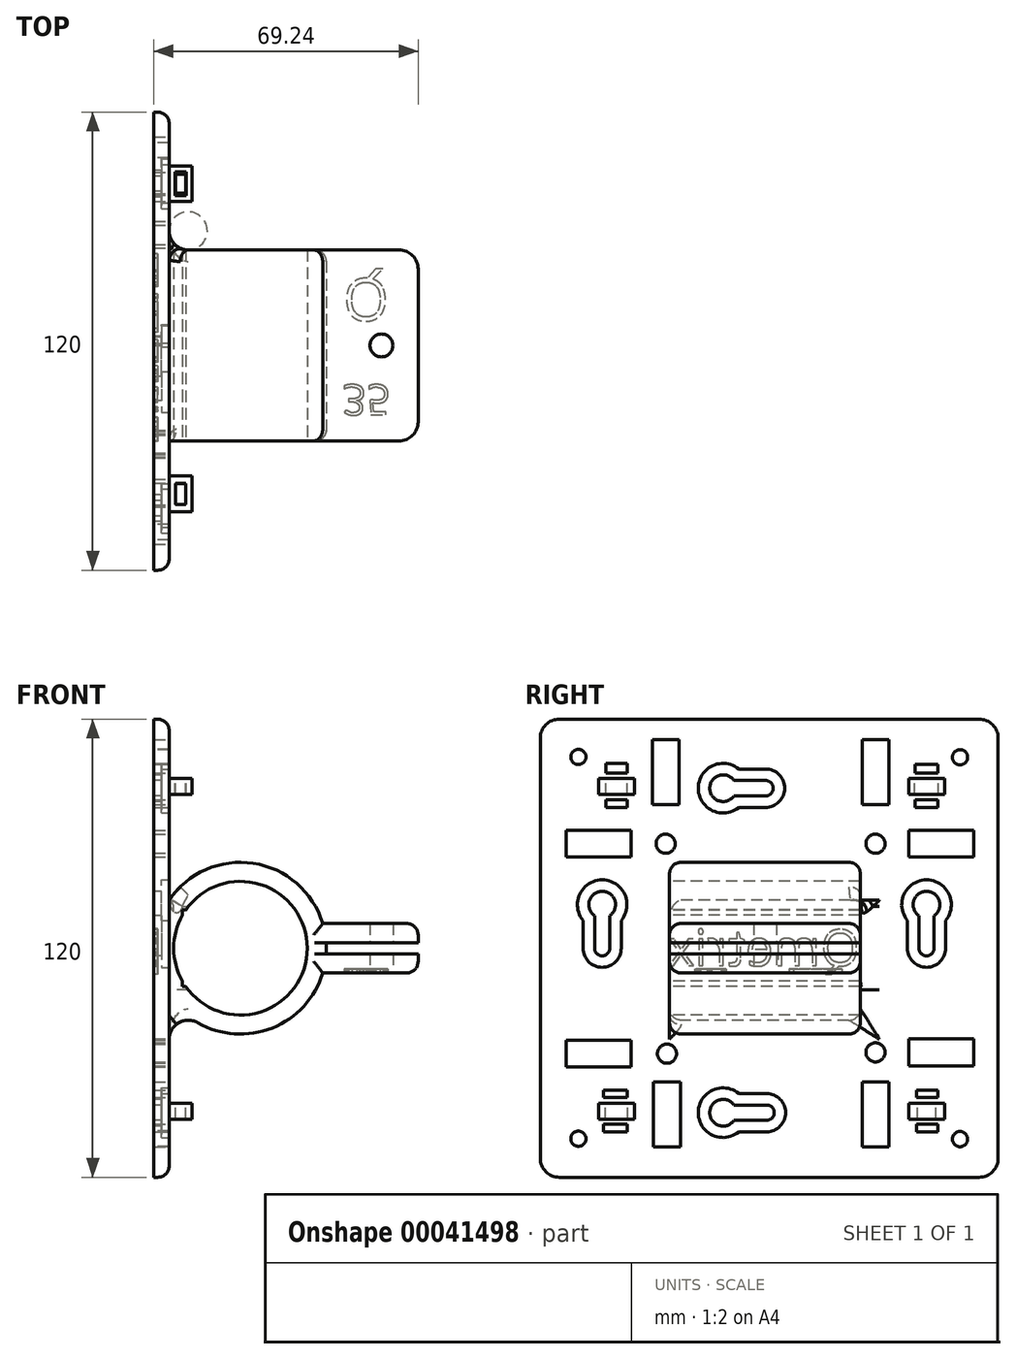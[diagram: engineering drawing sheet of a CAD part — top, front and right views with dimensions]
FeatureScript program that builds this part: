
annotation { "Feature Type Name" : "Feature", "Feature Type Description" : "" }
export const myFeature = defineFeature(function(context is Context, id is Id, definition is map)
    precondition{}
    {
        {
            var Q0;
            Q0=qCreatedBy(makeId("Top.planeOp"),FACE);
            var sketch = newSketch(context, id + "F0", { "sketchPlane" : qUnion([Q0])});
            skArc(sketch, "E0", {"start": v(-13.95, -1.23) * mm, "mid": v(13.99, 0.62) * mm, "end": v(-14, 0) * mm});
            skLineSegment(sketch, "E1.bottom", {"start": v(-14, 0) * mm, "end": v(-35.61, 0) * mm});
            skLineSegment(sketch, "E1.top", {"start": v(-17.8, 3.8) * mm, "end": v(-35.61, 3.8) * mm});
            skLineSegment(sketch, "E1.right", {"start": v(-35.61, 0) * mm, "end": v(-35.61, 3.8) * mm});
            skLineSegment(sketch, "E2.bottom", {"start": v(-13.95, -1.23) * mm, "end": v(-35.61, -1.23) * mm});
            skLineSegment(sketch, "E2.top", {"start": v(-17.57, -4.76) * mm, "end": v(-35.61, -4.76) * mm});
            skLineSegment(sketch, "E2.right", {"start": v(-35.61, -1.23) * mm, "end": v(-35.61, -4.76) * mm});
            skArc(sketch, "E3.trimOffspring", {"start": v(-17.57, -4.76) * mm, "mid": v(-1.54, -18.14) * mm, "end": v(16.51, -7.65) * mm});
            skLineSegment(sketch, "E4.bottom", {"start": v(16.51, 7.65) * mm, "end": v(17.36, 7.65) * mm});
            skLineSegment(sketch, "E4.top", {"start": v(16.51, -7.93) * mm, "end": v(17.36, -7.93) * mm});
            skLineSegment(sketch, "E4.left", {"start": v(16.51, -7.65) * mm, "end": v(16.51, -7.93) * mm});
            skLineSegment(sketch, "E4.right", {"start": v(17.36, 7.65) * mm, "end": v(17.36, -7.93) * mm});
            skArc(sketch, "E5.trimOffspring", {"start": v(16.51, 7.65) * mm, "mid": v(-2.03, 18.09) * mm, "end": v(-17.8, 3.8) * mm});
            skSolve(sketch);
        }
        {
            var Q0;
            Q0=makeQuery(id+"F0.imprint","IMPRINT",FACE,{"disambiguationData":[TD([[makeQuery(id+"F0.imprint","IMPRINT",EDGE,{"derivedFrom":sQuery(id+"F0.wireOp",EDGE,"E0")}),-1.0]])]});
            extrude(context, id + "F1", {"entities" : qUnion([Q0]), "depth" : 20 * mm});
        }
        {
            var Q0;
            Q0=makeQuery(id+"F1.opExtrude","SWEPT_FACE",FACE,{"disambiguationData":[OSD([sQuery(id+"F0.wireOp",EDGE,"E1.top")])]});
            var sketch = newSketch(context, id + "F2", { "sketchPlane" : qUnion([Q0])});
            skCircle(sketch, "E6", {"center": v(29.92, 10) * mm, "radius": 3 * mm});
            skPoint(sketch, "E6.centerSnap0", {"position": v(35.61, 10) * mm});
            skSolve(sketch);
        }
        {
            var Q0;
            Q0=makeQuery(id+"F2.imprint","IMPRINT",FACE,{"disambiguationData":[TD([[makeQuery(id+"F2.imprint","IMPRINT",EDGE,{"derivedFrom":sQuery(id+"F2.wireOp",EDGE,"E6")}),1.0]])]});
            extrude(context, id + "F3", {"entities" : qUnion([Q0]), "operationType" : NewBodyOperationType.REMOVE, "endBound" : BoundingType.THROUGH_ALL, "oppositeDirection" : true, "depth" : 25 * mm});
        }
        {
            var Q0;
            Q0=makeQuery(id+"F1.opExtrude","SWEPT_FACE",FACE,{"disambiguationData":[OSD([sQuery(id+"F0.wireOp",EDGE,"E4.bottom")])]});
            var sketch = newSketch(context, id + "F4", { "sketchPlane" : qUnion([Q0])});
            skCircle(sketch, "E7", {"center": v(-31.76, 10) * mm, "radius": 22.5 * mm});
            skPoint(sketch, "E7.centerSnap0", {"position": v(-17.36, 10) * mm});
            skCircle(sketch, "E8", {"center": v(-31.76, 10) * mm, "radius": 17.5 * mm});
            skSolve(sketch);
        }
        {
            var Q0;
            {var subQ0=sQuery(id+"F0.wireOp",EDGE,"E4.bottom");var subQ1=makeQuery(id+"F1.opExtrude","CAP_EDGE",EDGE,{"disambiguationData":[OSD([subQ0])],"isStart":true});var subQ9=sQuery(id+"F4.wireOp",EDGE,"E7");var subQ10=makeQuery(id+"F4.imprint","INTERSECT",VERTEX,{"derivedFrom":[subQ1,subQ9]});Q0=makeQuery(id+"F4.imprint","IMPRINT",FACE,{"disambiguationData":[TD([[makeQuery(id+"F4.imprint","IMPRINT",EDGE,{"disambiguationData":[TD([[subQ10,1.0]])],"derivedFrom":subQ9}),1.0]])]});}
            var Q1;
            {var subQ0=sQuery(id+"F0.wireOp",EDGE,"E4.bottom");var subQ7=makeQuery(id+"F1.opExtrude","CAP_EDGE",EDGE,{"disambiguationData":[OSD([subQ0])],"isStart":true});var subQ9=sQuery(id+"F4.wireOp",EDGE,"E7");var subQ10=makeQuery(id+"F4.imprint","INTERSECT",VERTEX,{"derivedFrom":[subQ7,subQ9]});Q1=makeQuery(id+"F4.imprint","IMPRINT",FACE,{"disambiguationData":[TD([[makeQuery(id+"F4.imprint","IMPRINT",EDGE,{"disambiguationData":[TD([[subQ10,-1.0]])],"derivedFrom":subQ9}),1.0]])]});}
            var Q2;
            Q2=sQuery(id+"F4.wireOp",EDGE,"E7");
            extrude(context, id + "F5", {"entities" : qUnion([Q0, Q1]), "operationType" : NewBodyOperationType.ADD, "surfaceEntities" : qUnion([Q2]), "depth" : 35 * mm, "symmetric" : true});
        }
        {
            var Q0;
            Q0=makeQuery(id+"F5.boolean.opBoolean","SPLIT",FACE,{"disambiguationData":[TD([makeQuery(id+"F1.opExtrude","SWEPT_FACE",FACE,{"disambiguationData":[OSD([sQuery(id+"F0.wireOp",EDGE,"E4.right")])]})])],"derivedFrom":makeQuery(id+"F1.opExtrude","SWEPT_FACE",FACE,{"disambiguationData":[OSD([sQuery(id+"F0.wireOp",EDGE,"E4.top")])]})});
            extrude(context, id + "F6", {"entities" : qUnion([Q0]), "operationType" : NewBodyOperationType.REMOVE, "oppositeDirection" : true, "depth" : 25 * mm});
        }
        {
            var Q0;
            Q0=makeQuery(id+"F5.opExtrude","CAP_FACE",FACE,{"disambiguationData":[OSD([sQuery(id+"F4.wireOp",EDGE,"E7"),sQuery(id+"F4.wireOp",EDGE,"E8")])],"isStart":true});
            var sketch = newSketch(context, id + "F7", { "sketchPlane" : qUnion([Q0])});
            skLineSegment(sketch, "E9.bottom", {"start": v(49.2, 8.53) * mm, "end": v(78.32, 8.53) * mm});
            skLineSegment(sketch, "E9.top", {"start": v(49.2, 3.53) * mm, "end": v(78.32, 3.53) * mm});
            skLineSegment(sketch, "E9.left", {"start": v(49.2, 8.53) * mm, "end": v(49.2, 3.53) * mm});
            skLineSegment(sketch, "E9.right", {"start": v(78.32, 8.53) * mm, "end": v(78.32, 3.53) * mm});
            skPoint(sketch, "E10.oppositeSnap0", {"position": v(78.32, 6.03) * mm});
            skLineSegment(sketch, "E10.bottom", {"start": v(49.2, 11.47) * mm, "end": v(78.32, 11.47) * mm});
            skLineSegment(sketch, "E10.top", {"start": v(49.2, 16.47) * mm, "end": v(78.32, 16.47) * mm});
            skLineSegment(sketch, "E10.left", {"start": v(49.2, 11.47) * mm, "end": v(49.2, 16.47) * mm});
            skLineSegment(sketch, "E10.right", {"start": v(78.32, 11.47) * mm, "end": v(78.32, 16.47) * mm});
            skLineSegment(sketch, "E11.bottom", {"start": v(56.42, 8.53) * mm, "end": v(46.21, 8.53) * mm});
            skLineSegment(sketch, "E11.top", {"start": v(56.42, 11.47) * mm, "end": v(46.21, 11.47) * mm});
            skLineSegment(sketch, "E11.left", {"start": v(56.42, 8.53) * mm, "end": v(56.42, 11.47) * mm});
            skLineSegment(sketch, "E11.right", {"start": v(46.21, 8.53) * mm, "end": v(46.21, 11.47) * mm});
            skSolve(sketch);
        }
        {
            var Q0;
            {var subQ0=sQuery(id+"F7.wireOp",EDGE,"E11.bottom");var subQ3=makeQuery(id+"F5.opExtrude","CAP_EDGE",EDGE,{"disambiguationData":[OSD([sQuery(id+"F4.wireOp",EDGE,"E7")])],"isStart":true});var subQ4=makeQuery(id+"F7.imprint","INTERSECT",VERTEX,{"derivedFrom":[subQ3,subQ0]});Q0=makeQuery(id+"F7.imprint","IMPRINT",FACE,{"disambiguationData":[TD([[makeQuery(id+"F7.imprint","IMPRINT",EDGE,{"disambiguationData":[TD([[subQ4,1.0]])],"derivedFrom":subQ3}),-1.0]])]});}
            var Q1;
            Q1=makeQuery(id+"F5.opExtrude","CAP_FACE",FACE,{"disambiguationData":[OSD([sQuery(id+"F4.wireOp",EDGE,"E7"),sQuery(id+"F4.wireOp",EDGE,"E8")])],"isStart":false});
            extrude(context, id + "F8", {"entities" : qUnion([Q0]), "operationType" : NewBodyOperationType.REMOVE, "endBound" : BoundingType.UP_TO_SURFACE, "oppositeDirection" : true, "endBoundEntityFace" : qUnion([Q1]), "depth" : 25 * mm});
        }
        {
            var Q0;
            {var subQ0=sQuery(id+"F7.wireOp",EDGE,"E9.right");Q0=makeQuery(id+"F7.imprint","IMPRINT",FACE,{"disambiguationData":[TD([[makeQuery(id+"F7.imprint","IMPRINT",EDGE,{"derivedFrom":subQ0}),-1.0]])]});}
            var Q1;
            {var subQ0=sQuery(id+"F7.wireOp",EDGE,"E10.right");Q1=makeQuery(id+"F7.imprint","IMPRINT",FACE,{"disambiguationData":[TD([[makeQuery(id+"F7.imprint","IMPRINT",EDGE,{"derivedFrom":subQ0}),1.0]])]});}
            var Q2;
            Q2=makeQuery(id+"F5.opExtrude","CAP_FACE",FACE,{"disambiguationData":[OSD([sQuery(id+"F4.wireOp",EDGE,"E7"),sQuery(id+"F4.wireOp",EDGE,"E8")])],"isStart":false});
            extrude(context, id + "F9", {"entities" : qUnion([Q0, Q1]), "operationType" : NewBodyOperationType.ADD, "endBound" : BoundingType.UP_TO_SURFACE, "oppositeDirection" : true, "endBoundEntityFace" : qUnion([Q2]), "depth" : 25 * mm});
        }
        {
            var Q0;
            {var subQ0=sQuery(id+"F7.wireOp",EDGE,"E11.top");var subQ1=sQuery(id+"F4.wireOp",EDGE,"E7");var subQ2=sQuery(id+"F4.wireOp",EDGE,"E8");var subQ3=sQuery(id+"F0.wireOp",EDGE,"E4.right");var subQ4=sQuery(id+"F0.wireOp",EDGE,"E4.bottom");var subQ9=sQuery(id+"F0.wireOp",EDGE,"E3.trimOffspring");var subQ10=makeQuery(id+"F1.opExtrude","SWEPT_FACE",FACE,{"disambiguationData":[OSD([subQ9])]});var subQ12=sQuery(id+"F0.wireOp",EDGE,"E5.trimOffspring");var subQ36=makeQuery(id+"F5.boolean.opBoolean","SPLIT",FACE,{"disambiguationData":[TD([subQ10])],"derivedFrom":makeQuery(id+"F5.opExtrude","CAP_FACE",FACE,{"disambiguationData":[OSD([subQ4,subQ3,subQ12,subQ1,subQ2])],"isStart":true})});var subQ37=sQuery(id+"F7.wireOp",EDGE,"E11.bottom");Q0=qUnion([makeQuery(id+"F9.boolean.opBoolean","MERGE",FACE,{"derivedFrom":[makeQuery(id+"F8.boolean.opBoolean","SPLIT",FACE,{"disambiguationData":[TD([makeQuery(id+"F8.opExtrude","SWEPT_FACE",FACE,{"disambiguationData":[OSD([subQ37])]})])],"derivedFrom":subQ36}),makeQuery(id+"F9.opExtrude","CAP_FACE",FACE,{"disambiguationData":[OSD([subQ1,sQuery(id+"F7.wireOp",EDGE,"E9.bottom"),sQuery(id+"F7.wireOp",EDGE,"E9.top"),sQuery(id+"F7.wireOp",EDGE,"E9.right"),subQ37])],"isStart":true})]}),makeQuery(id+"F9.boolean.opBoolean","MERGE",FACE,{"derivedFrom":[makeQuery(id+"F8.boolean.opBoolean","SPLIT",FACE,{"disambiguationData":[TD([makeQuery(id+"F8.opExtrude","SWEPT_FACE",FACE,{"disambiguationData":[OSD([subQ0])]})])],"derivedFrom":subQ36}),makeQuery(id+"F9.opExtrude","CAP_FACE",FACE,{"disambiguationData":[OSD([subQ1,sQuery(id+"F7.wireOp",EDGE,"E10.bottom"),sQuery(id+"F7.wireOp",EDGE,"E10.top"),sQuery(id+"F7.wireOp",EDGE,"E10.right"),subQ0])],"isStart":true})]})]);}
            extrude(context, id + "F10", {"entities" : qUnion([Q0]), "operationType" : NewBodyOperationType.ADD, "depth" : 15 * mm});
        }
        {
            var Q0;
            {var subQ0=sQuery(id+"F7.wireOp",EDGE,"E9.top");Q0=makeQuery(id+"F10.boolean.opBoolean","MERGE",FACE,{"derivedFrom":[makeQuery(id+"F9.opExtrude","SWEPT_FACE",FACE,{"disambiguationData":[OSD([subQ0])]}),makeQuery(id+"F10.opExtrude","SWEPT_FACE",FACE,{"disambiguationData":[OSD([subQ0])]})]});}
            var sketch = newSketch(context, id + "F11", { "sketchPlane" : qUnion([Q0])});
            skCircle(sketch, "E12", {"center": v(68.71, -0.15) * mm, "radius": 3 * mm});
            skPoint(sketch, "E12.centerSnap0", {"position": v(78.32, -0.15) * mm});
            skSolve(sketch);
        }
        {
            var Q0;
            Q0=makeQuery(id+"F1.opExtrude","CAP_EDGE",EDGE,{"disambiguationData":[OSD([sQuery(id+"F0.wireOp",EDGE,"E2.right")])],"isStart":true});
            var Q1;
            Q1=makeQuery(id+"F1.opExtrude","CAP_EDGE",EDGE,{"disambiguationData":[OSD([sQuery(id+"F0.wireOp",EDGE,"E1.right")])],"isStart":true});
            var Q2;
            Q2=makeQuery(id+"F1.opExtrude","CAP_EDGE",EDGE,{"disambiguationData":[OSD([sQuery(id+"F0.wireOp",EDGE,"E2.right")])],"isStart":false});
            var Q3;
            Q3=makeQuery(id+"F1.opExtrude","CAP_EDGE",EDGE,{"disambiguationData":[OSD([sQuery(id+"F0.wireOp",EDGE,"E1.right")])],"isStart":false});
            var Q4;
            Q4=makeQuery(id+"F9.opExtrude","CAP_EDGE",EDGE,{"disambiguationData":[OSD([sQuery(id+"F7.wireOp",EDGE,"E9.right")])],"isStart":true});
            var Q5;
            Q5=makeQuery(id+"F9.opExtrude","CAP_EDGE",EDGE,{"disambiguationData":[OSD([sQuery(id+"F7.wireOp",EDGE,"E10.right")])],"isStart":true});
            var Q6;
            Q6=makeQuery(id+"F9.opExtrude","CAP_EDGE",EDGE,{"disambiguationData":[OSD([sQuery(id+"F7.wireOp",EDGE,"E10.right")])],"isStart":false});
            var Q7;
            Q7=makeQuery(id+"F9.opExtrude","CAP_EDGE",EDGE,{"disambiguationData":[OSD([sQuery(id+"F7.wireOp",EDGE,"E9.right")])],"isStart":false});
            var Q8;
            Q8=makeQuery(id+"F10.opExtrude","CAP_EDGE",EDGE,{"disambiguationData":[OSD([sQuery(id+"F7.wireOp",EDGE,"E9.right")])],"isStart":false});
            var Q9;
            Q9=makeQuery(id+"F10.opExtrude","CAP_EDGE",EDGE,{"disambiguationData":[OSD([sQuery(id+"F7.wireOp",EDGE,"E10.right")])],"isStart":false});
            fillet(context, id + "F12", {"entities" : qUnion([Q0, Q1, Q2, Q3, Q4, Q5, Q6, Q7, Q8, Q9]), "radius" : 5 * mm, "tangentPropagation" : true, "allowEdgeOverflow" : false});
        }
        {
            var Q0;
            {var subQ0=sQuery(id+"F7.wireOp",EDGE,"E9.top");Q0=makeQuery(id+"F10.boolean.opBoolean","MERGE",FACE,{"derivedFrom":[makeQuery(id+"F9.opExtrude","SWEPT_FACE",FACE,{"disambiguationData":[OSD([subQ0])]}),makeQuery(id+"F10.opExtrude","SWEPT_FACE",FACE,{"disambiguationData":[OSD([subQ0])]})]});}
            var sketch = newSketch(context, id + "F13", { "sketchPlane" : qUnion([Q0])});
            skText(sketch, "E13", { "text": "35", "fontName": "OpenSans-Regular.ttf"});
            skText(sketch, "E14", { "text": "Q", "fontName": "OpenSans-Regular.ttf"});
            const initialGuessF13  = {"E13": [0.0584, 0.01015, 1, 0, 0.00796], "E14": [0.05865, -0.01766, 1, 0, 0.0111]};
            skSetInitialGuess(sketch, initialGuessF13);
            skSolve(sketch);
        }
        {
            var Q0;
            Q0=makeQuery(id+"F0.imprint","IMPRINT",FACE,{"disambiguationData":[TD([[makeQuery(id+"F0.imprint","IMPRINT",EDGE,{"derivedFrom":sQuery(id+"F0.wireOp",EDGE,"E0")}),-1.0]])]});
            var sketch = newSketch(context, id + "F14", { "sketchPlane" : qUnion([Q0])});
            skLineSegment(sketch, "E15.bottom", {"start": v(13.08, 61.27) * mm, "end": v(9.08, 61.27) * mm});
            skLineSegment(sketch, "E15.top", {"start": v(13.08, -58.73) * mm, "end": v(9.08, -58.73) * mm});
            skLineSegment(sketch, "E15.left", {"start": v(13.08, 61.27) * mm, "end": v(13.08, -58.73) * mm});
            skLineSegment(sketch, "E15.right", {"start": v(9.08, 61.27) * mm, "end": v(9.08, -58.73) * mm});
            skSolve(sketch);
        }
        {
            var Q0;
            Q0=makeQuery(id+"F0.imprint","IMPRINT",FACE,{"disambiguationData":[TD([[makeQuery(id+"F0.imprint","IMPRINT",EDGE,{"derivedFrom":sQuery(id+"F0.wireOp",EDGE,"E0")}),-1.0]])]});
            extrude(context, id + "F15", {"entities" : qUnion([Q0]), "operationType" : NewBodyOperationType.REMOVE, "depth" : 25 * mm});
        }
        {
            var Q0;
            {var subQ0=sQuery(id+"F14.wireOp",EDGE,"E15.top");Q0=makeQuery(id+"F14.imprint","IMPRINT",FACE,{"disambiguationData":[TD([[makeQuery(id+"F14.imprint","IMPRINT",EDGE,{"derivedFrom":subQ0}),-1.0]])]});}
            var Q1;
            {var subQ0=sQuery(id+"F14.wireOp",EDGE,"E15.bottom");Q1=makeQuery(id+"F14.imprint","IMPRINT",FACE,{"disambiguationData":[TD([[makeQuery(id+"F14.imprint","IMPRINT",EDGE,{"derivedFrom":subQ0}),1.0]])]});}
            var Q2;
            {var subQ0=sQuery(id+"F14.wireOp",EDGE,"E15.left");var subQ1=makeQuery(id+"F0.imprint","IMPRINT",EDGE,{"derivedFrom":sQuery(id+"F0.wireOp",EDGE,"E4.bottom")});var subQ2=makeQuery(id+"F14.imprint","INTERSECT",VERTEX,{"derivedFrom":[subQ1,subQ0]});Q2=makeQuery(id+"F14.imprint","IMPRINT",FACE,{"disambiguationData":[TD([[makeQuery(id+"F14.imprint","IMPRINT",EDGE,{"disambiguationData":[TD([[subQ2,-1.0]])],"derivedFrom":subQ0}),-1.0]])]});}
            extrude(context, id + "F16", {"entities" : qUnion([Q0, Q1, Q2]), "operationType" : NewBodyOperationType.ADD, "depth" : 70 * mm, "hasSecondDirection" : true, "secondDirectionOppositeDirection" : true, "secondDirectionDepth" : 50 * mm});
        }
        {
            var Q0;
            Q0=makeQuery(id+"F16.opExtrude","CAP_EDGE",EDGE,{"disambiguationData":[OSD([sQuery(id+"F14.wireOp",EDGE,"E15.bottom")])],"isStart":false});
            var Q1;
            Q1=makeQuery(id+"F16.opExtrude","CAP_EDGE",EDGE,{"disambiguationData":[OSD([sQuery(id+"F14.wireOp",EDGE,"E15.bottom")])],"isStart":true});
            var Q2;
            Q2=makeQuery(id+"F16.opExtrude","CAP_EDGE",EDGE,{"disambiguationData":[OSD([sQuery(id+"F14.wireOp",EDGE,"E15.top")])],"isStart":true});
            var Q3;
            Q3=makeQuery(id+"F16.opExtrude","CAP_EDGE",EDGE,{"disambiguationData":[OSD([sQuery(id+"F14.wireOp",EDGE,"E15.top")])],"isStart":false});
            fillet(context, id + "F17", {"entities" : qUnion([Q0, Q1, Q2, Q3]), "radius" : 5 * mm, "tangentPropagation" : true, "allowEdgeOverflow" : false});
        }
        {
            var Q0;
            Q0=makeQuery(id+"F16.opExtrude","SWEPT_FACE",FACE,{"disambiguationData":[OSD([sQuery(id+"F14.wireOp",EDGE,"E15.right")])]});
            var sketch = newSketch(context, id + "F18", { "sketchPlane" : qUnion([Q0])});
            skCircle(sketch, "E16", {"center": v(-51.27, -40) * mm, "radius": 2 * mm});
            skCircle(sketch, "E17", {"center": v(-51.27, 60) * mm, "radius": 2 * mm});
            skCircle(sketch, "E18", {"center": v(48.73, -39.9) * mm, "radius": 2 * mm});
            skCircle(sketch, "E19", {"center": v(48.73, 60.1) * mm, "radius": 2 * mm});
            skLineSegment(sketch, "E20", {"start": v(-82.64, 10) * mm, "end": v(82.64, 10) * mm, "construction": true});
            skArc(sketch, "E21", {"start": v(-44.5, 10) * mm, "mid": v(-42.5, 8) * mm, "end": v(-40.5, 10) * mm});
            skArc(sketch, "E22", {"start": v(40.5, 10) * mm, "mid": v(42.5, 8) * mm, "end": v(44.5, 10) * mm});
            skLineSegment(sketch, "E23", {"start": v(-82.64, 21.4) * mm, "end": v(68.31, 21.4) * mm, "construction": true});
            skArc(sketch, "E24", {"start": v(-40.5, 18.53) * mm, "mid": v(-42.5, 24.9) * mm, "end": v(-44.5, 18.53) * mm});
            skArc(sketch, "E25", {"start": v(44.5, 18.53) * mm, "mid": v(42.5, 24.9) * mm, "end": v(40.5, 18.53) * mm});
            skLineSegment(sketch, "E26", {"start": v(-44.5, 10) * mm, "end": v(-44.5, 18.53) * mm});
            skLineSegment(sketch, "E27", {"start": v(-40.5, 10) * mm, "end": v(-40.5, 18.53) * mm});
            skLineSegment(sketch, "E28", {"start": v(40.5, 10) * mm, "end": v(40.5, 18.53) * mm});
            skLineSegment(sketch, "E29", {"start": v(44.5, 10) * mm, "end": v(44.5, 18.53) * mm});
            skLineSegment(sketch, "E30.1.0", {"start": v(0, 53.91) * mm, "end": v(7.95, 53.91) * mm});
            skArc(sketch, "E30.1.1", {"start": v(7.95, 49.91) * mm, "mid": v(14.32, 51.91) * mm, "end": v(7.95, 53.91) * mm});
            skLineSegment(sketch, "E30.1.2", {"start": v(-0.59, 49.91) * mm, "end": v(7.95, 49.91) * mm});
            skArc(sketch, "E30.1.3", {"start": v(0, 53.91) * mm, "mid": v(-2.3, 52.2) * mm, "end": v(-0.59, 49.91) * mm});
            skArc(sketch, "E30.1.12", {"start": v(-0.59, -31.09) * mm, "mid": v(-2.59, -33.09) * mm, "end": v(-0.59, -35.09) * mm});
            skLineSegment(sketch, "E30.1.13", {"start": v(-0.59, -31.09) * mm, "end": v(7.95, -31.09) * mm});
            skLineSegment(sketch, "E30.1.14", {"start": v(-0.59, -35.09) * mm, "end": v(7.95, -35.09) * mm});
            skArc(sketch, "E30.1.15", {"start": v(7.95, -35.09) * mm, "mid": v(14.32, -33.09) * mm, "end": v(7.95, -31.09) * mm});
            skPoint(sketch, "E30.center", {"position": v(0, 10) * mm});
            skLineSegment(sketch, "E30.anchor1", {"start": v(0, 10) * mm, "end": v(-44.5, 10) * mm, "construction": true});
            skLineSegment(sketch, "E30.anchor2", {"start": v(0, 10) * mm, "end": v(0, 53.91) * mm, "construction": true});
            skPoint(sketch, "E31.MirrorCS.end.orphan", {"position": v(-44.5, -18.53) * mm});
            skPoint(sketch, "E31.MirrorCS.start.orphan", {"position": v(-40.5, -18.53) * mm});
            skPoint(sketch, "E32.MirrorCS.start.orphan", {"position": v(-44.5, -10) * mm});
            skPoint(sketch, "E33.MirrorCS.start.orphan", {"position": v(-40.5, -10) * mm});
            skPoint(sketch, "E34.MirrorCS.end.orphan", {"position": v(40.5, -18.53) * mm});
            skPoint(sketch, "E34.MirrorCS.start.orphan", {"position": v(44.5, -18.53) * mm});
            skPoint(sketch, "E35.MirrorCS.start.orphan", {"position": v(44.5, -10) * mm});
            skPoint(sketch, "E36.MirrorCS.start.orphan", {"position": v(40.5, -10) * mm});
            skCircle(sketch, "E37.1.0.0", {"center": v(-26.27, -40) * mm, "radius": 2 * mm});
            skCircle(sketch, "E37.2.0.0", {"center": v(-1.27, -40) * mm, "radius": 2 * mm});
            skCircle(sketch, "E37.3.0.0", {"center": v(23.73, -40) * mm, "radius": 2 * mm});
            skLineSegment(sketch, "E37.direction1", {"start": v(-51.27, -40) * mm, "end": v(-26.27, -40) * mm, "construction": true});
            skCircle(sketch, "E38.0.1.0", {"center": v(-51.27, -15) * mm, "radius": 2 * mm});
            skCircle(sketch, "E38.0.2.0", {"center": v(-51.27, 10) * mm, "radius": 2 * mm});
            skCircle(sketch, "E38.0.3.0", {"center": v(-51.27, 35) * mm, "radius": 2 * mm});
            skLineSegment(sketch, "E38.direction2", {"start": v(-51.27, -40) * mm, "end": v(-51.27, -15) * mm, "construction": true});
            skSolve(sketch);
        }
        {
            var Q0;
            Q0=makeQuery(id+"F18.imprint","IMPRINT",FACE,{"disambiguationData":[TD([[makeQuery(id+"F18.imprint","IMPRINT",EDGE,{"derivedFrom":sQuery(id+"F18.wireOp",EDGE,"E18")}),1.0]])]});
            var Q1;
            Q1=makeQuery(id+"F18.imprint","IMPRINT",FACE,{"disambiguationData":[TD([[makeQuery(id+"F18.imprint","IMPRINT",EDGE,{"derivedFrom":sQuery(id+"F18.wireOp",EDGE,"E16")}),1.0]])]});
            var Q2;
            Q2=makeQuery(id+"F18.imprint","IMPRINT",FACE,{"disambiguationData":[TD([[makeQuery(id+"F18.imprint","IMPRINT",EDGE,{"derivedFrom":sQuery(id+"F18.wireOp",EDGE,"E17")}),1.0]])]});
            var Q3;
            Q3=makeQuery(id+"F18.imprint","IMPRINT",FACE,{"disambiguationData":[TD([[makeQuery(id+"F18.imprint","IMPRINT",EDGE,{"derivedFrom":sQuery(id+"F18.wireOp",EDGE,"E19")}),1.0]])]});
            var Q4;
            Q4=makeQuery(id+"F18.imprint","IMPRINT",FACE,{"disambiguationData":[TD([[makeQuery(id+"F18.imprint","IMPRINT",EDGE,{"derivedFrom":sQuery(id+"F18.wireOp",EDGE,"E21")}),1.0]])]});
            var Q5;
            Q5=makeQuery(id+"F18.imprint","IMPRINT",FACE,{"disambiguationData":[TD([[makeQuery(id+"F18.imprint","IMPRINT",EDGE,{"derivedFrom":sQuery(id+"F18.wireOp",EDGE,"E30.1.12")}),1.0]])]});
            var Q6;
            Q6=makeQuery(id+"F18.imprint","IMPRINT",FACE,{"disambiguationData":[TD([[makeQuery(id+"F18.imprint","IMPRINT",EDGE,{"derivedFrom":sQuery(id+"F18.wireOp",EDGE,"E22")}),1.0]])]});
            var Q7;
            Q7=makeQuery(id+"F18.imprint","IMPRINT",FACE,{"disambiguationData":[TD([[makeQuery(id+"F18.imprint","IMPRINT",EDGE,{"derivedFrom":sQuery(id+"F18.wireOp",EDGE,"E30.1.0")}),-1.0]])]});
            var Q8;
            Q8=sQuery(id+"F18.wireOp",EDGE,"E16");
            var Q9;
            Q9=sQuery(id+"F18.wireOp",EDGE,"E17");
            var Q10;
            Q10=sQuery(id+"F18.wireOp",EDGE,"E19");
            var Q11;
            Q11=sQuery(id+"F18.wireOp",EDGE,"E18");
            extrude(context, id + "F19", {"entities" : qUnion([Q0, Q1, Q2, Q3, Q4, Q5, Q6, Q7]), "operationType" : NewBodyOperationType.REMOVE, "surfaceEntities" : qUnion([Q8, Q9, Q10, Q11]), "oppositeDirection" : true, "depth" : 25 * mm});
        }
        {
            var Q0;
            {var subQ0=sQuery(id+"F4.wireOp",EDGE,"E7");Q0=makeQuery(id+"F9.boolean.opBoolean","MERGE",FACE,{"derivedFrom":[makeQuery(id+"F5.opExtrude","CAP_FACE",FACE,{"disambiguationData":[OSD([sQuery(id+"F0.wireOp",EDGE,"E4.bottom"),sQuery(id+"F0.wireOp",EDGE,"E4.right"),sQuery(id+"F0.wireOp",EDGE,"E5.trimOffspring"),subQ0,sQuery(id+"F4.wireOp",EDGE,"E8")])],"isStart":false}),makeQuery(id+"F9.opExtrude","CAP_FACE",FACE,{"disambiguationData":[OSD([subQ0,sQuery(id+"F7.wireOp",EDGE,"E9.bottom"),sQuery(id+"F7.wireOp",EDGE,"E9.top"),sQuery(id+"F7.wireOp",EDGE,"E9.right"),sQuery(id+"F7.wireOp",EDGE,"E11.bottom")])],"isStart":false}),makeQuery(id+"F9.opExtrude","CAP_FACE",FACE,{"disambiguationData":[OSD([subQ0,sQuery(id+"F7.wireOp",EDGE,"E10.bottom"),sQuery(id+"F7.wireOp",EDGE,"E10.top"),sQuery(id+"F7.wireOp",EDGE,"E10.right"),sQuery(id+"F7.wireOp",EDGE,"E11.top")])],"isStart":false})]});}
            var Q1;
            Q1=makeQuery(id+"F10.opExtrude","CAP_FACE",FACE,{"disambiguationData":[OSD([sQuery(id+"F0.wireOp",EDGE,"E4.bottom"),sQuery(id+"F0.wireOp",EDGE,"E4.right"),sQuery(id+"F0.wireOp",EDGE,"E5.trimOffspring"),sQuery(id+"F4.wireOp",EDGE,"E7"),sQuery(id+"F4.wireOp",EDGE,"E8"),sQuery(id+"F7.wireOp",EDGE,"E9.bottom"),sQuery(id+"F7.wireOp",EDGE,"E9.top"),sQuery(id+"F7.wireOp",EDGE,"E9.right"),sQuery(id+"F7.wireOp",EDGE,"E11.bottom")])],"isStart":false});
            extrude(context, id + "F20", {"entities" : qUnion([Q0]), "operationType" : NewBodyOperationType.ADD, "endBound" : BoundingType.UP_TO_SURFACE, "oppositeDirection" : true, "endBoundEntityFace" : qUnion([Q1]), "depth" : 25 * mm});
        }
        {
            var Q0;
            {var subQ0=sQuery(id+"F14.wireOp",EDGE,"E15.left");var subQ1=sQuery(id+"F7.wireOp",EDGE,"E11.top");var subQ2=sQuery(id+"F7.wireOp",EDGE,"E11.bottom");var subQ3=sQuery(id+"F7.wireOp",EDGE,"E10.right");var subQ4=sQuery(id+"F7.wireOp",EDGE,"E10.top");var subQ5=sQuery(id+"F7.wireOp",EDGE,"E10.bottom");var subQ6=sQuery(id+"F7.wireOp",EDGE,"E9.right");var subQ7=sQuery(id+"F7.wireOp",EDGE,"E9.top");var subQ8=sQuery(id+"F7.wireOp",EDGE,"E9.bottom");var subQ9=sQuery(id+"F4.wireOp",EDGE,"E8");var subQ10=sQuery(id+"F4.wireOp",EDGE,"E7");var subQ11=sQuery(id+"F0.wireOp",EDGE,"E5.trimOffspring");var subQ12=sQuery(id+"F0.wireOp",EDGE,"E4.right");var subQ13=sQuery(id+"F0.wireOp",EDGE,"E4.bottom");var subQ14=makeQuery(id+"F16.opExtrude","SWEPT_FACE",FACE,{"disambiguationData":[OSD([subQ0])]});Q0=makeQuery(id+"F20.boolean.opBoolean","MERGE",EDGE,{"derivedFrom":[makeQuery(id+"F16.boolean.opBoolean","INTERSECT",EDGE,{"derivedFrom":[makeQuery(id+"F10.opExtrude","CAP_FACE",FACE,{"disambiguationData":[OSD([subQ13,subQ12,subQ11,subQ10,subQ9,subQ8,subQ7,subQ6,subQ2])],"isStart":false}),subQ14]}),makeQuery(id+"F16.boolean.opBoolean","INTERSECT",EDGE,{"derivedFrom":[makeQuery(id+"F10.opExtrude","CAP_FACE",FACE,{"disambiguationData":[OSD([subQ13,subQ12,subQ11,subQ10,subQ9,subQ5,subQ4,subQ3,subQ1])],"isStart":false}),subQ14]}),makeQuery(id+"F20.opExtrude","CAP_EDGE",EDGE,{"disambiguationData":[OSD([subQ13,subQ12,subQ11,subQ10,subQ9,subQ8,subQ7,subQ6,subQ5,subQ4,subQ3,subQ2,subQ1,subQ0])],"isStart":false})]});}
            var Q1;
            {var subQ0=sQuery(id+"F4.wireOp",EDGE,"E7");Q1=makeQuery(id+"F16.boolean.opBoolean","INTERSECT",EDGE,{"derivedFrom":[makeQuery(id+"F9.boolean.opBoolean","MERGE",FACE,{"derivedFrom":[makeQuery(id+"F5.opExtrude","CAP_FACE",FACE,{"disambiguationData":[OSD([sQuery(id+"F0.wireOp",EDGE,"E4.bottom"),sQuery(id+"F0.wireOp",EDGE,"E4.right"),sQuery(id+"F0.wireOp",EDGE,"E5.trimOffspring"),subQ0,sQuery(id+"F4.wireOp",EDGE,"E8")])],"isStart":false}),makeQuery(id+"F9.opExtrude","CAP_FACE",FACE,{"disambiguationData":[OSD([subQ0,sQuery(id+"F7.wireOp",EDGE,"E9.bottom"),sQuery(id+"F7.wireOp",EDGE,"E9.top"),sQuery(id+"F7.wireOp",EDGE,"E9.right"),sQuery(id+"F7.wireOp",EDGE,"E11.bottom")])],"isStart":false}),makeQuery(id+"F9.opExtrude","CAP_FACE",FACE,{"disambiguationData":[OSD([subQ0,sQuery(id+"F7.wireOp",EDGE,"E10.bottom"),sQuery(id+"F7.wireOp",EDGE,"E10.top"),sQuery(id+"F7.wireOp",EDGE,"E10.right"),sQuery(id+"F7.wireOp",EDGE,"E11.top")])],"isStart":false})]}),makeQuery(id+"F16.opExtrude","SWEPT_FACE",FACE,{"disambiguationData":[OSD([sQuery(id+"F14.wireOp",EDGE,"E15.left")])]})]});}
            var Q2;
            {var subQ0=sQuery(id+"F0.wireOp",EDGE,"E5.trimOffspring");var subQ1=sQuery(id+"F0.wireOp",EDGE,"E4.right");var subQ2=sQuery(id+"F0.wireOp",EDGE,"E4.left");var subQ3=sQuery(id+"F0.wireOp",EDGE,"E4.top");var subQ4=sQuery(id+"F0.wireOp",EDGE,"E4.bottom");var subQ5=sQuery(id+"F0.wireOp",EDGE,"E3.trimOffspring");var subQ6=sQuery(id+"F0.wireOp",EDGE,"E2.right");var subQ7=sQuery(id+"F0.wireOp",EDGE,"E2.top");var subQ8=sQuery(id+"F0.wireOp",EDGE,"E2.bottom");var subQ9=sQuery(id+"F0.wireOp",EDGE,"E1.right");var subQ10=sQuery(id+"F0.wireOp",EDGE,"E1.top");var subQ11=sQuery(id+"F0.wireOp",EDGE,"E1.bottom");var subQ12=sQuery(id+"F0.wireOp",EDGE,"E0");var subQ14=sQuery(id+"F4.wireOp",EDGE,"E7");var subQ15=makeQuery(id+"F5.opExtrude","SWEPT_FACE",FACE,{"disambiguationData":[OSD([subQ14])]});var subQ17=makeQuery(id+"F1.opExtrude","CAP_FACE",FACE,{"disambiguationData":[OSD([subQ12,subQ11,subQ10,subQ9,subQ8,subQ7,subQ6,subQ5,subQ4,subQ3,subQ2,subQ1,subQ0])],"isStart":true});var subQ18=makeQuery(id+"F5.boolean.opBoolean","SPLIT",EDGE,{"disambiguationData":[TD([subQ17])],"derivedFrom":makeQuery(id+"F5.opExtrude","CAP_EDGE",EDGE,{"disambiguationData":[OSD([subQ14])],"isStart":true})});Q2=makeQuery(id+"F16.boolean.opBoolean","INTERSECT",EDGE,{"disambiguationData":[OD(1.0)],"derivedFrom":[makeQuery(id+"F10.boolean.opBoolean","MERGE",FACE,{"derivedFrom":[subQ15,makeQuery(id+"F10.opExtrude","SWEPT_FACE",FACE,{"disambiguationData":[OSD([subQ14]),TDD([makeQuery(id+"F8.boolean.opBoolean","SPLIT",EDGE,{"disambiguationData":[TD([makeQuery(id+"F8.opExtrude","SWEPT_FACE",FACE,{"disambiguationData":[OSD([sQuery(id+"F7.wireOp",EDGE,"E11.bottom")])]})])],"derivedFrom":subQ18})])]}),makeQuery(id+"F10.opExtrude","SWEPT_FACE",FACE,{"disambiguationData":[OSD([subQ14]),TDD([makeQuery(id+"F8.boolean.opBoolean","SPLIT",EDGE,{"disambiguationData":[TD([makeQuery(id+"F8.opExtrude","SWEPT_FACE",FACE,{"disambiguationData":[OSD([sQuery(id+"F7.wireOp",EDGE,"E11.top")])]})])],"derivedFrom":subQ18})])]})]}),makeQuery(id+"F16.opExtrude","SWEPT_FACE",FACE,{"disambiguationData":[OSD([sQuery(id+"F14.wireOp",EDGE,"E15.left")])]})]});}
            var Q3;
            {var subQ0=sQuery(id+"F14.wireOp",EDGE,"E15.left");var subQ1=makeQuery(id+"F16.opExtrude","SWEPT_FACE",FACE,{"disambiguationData":[OSD([subQ0])]});var subQ2=sQuery(id+"F0.wireOp",EDGE,"E5.trimOffspring");var subQ3=sQuery(id+"F0.wireOp",EDGE,"E4.right");var subQ4=sQuery(id+"F0.wireOp",EDGE,"E4.left");var subQ5=sQuery(id+"F0.wireOp",EDGE,"E4.top");var subQ6=sQuery(id+"F0.wireOp",EDGE,"E4.bottom");var subQ7=sQuery(id+"F0.wireOp",EDGE,"E3.trimOffspring");var subQ8=sQuery(id+"F0.wireOp",EDGE,"E2.right");var subQ9=sQuery(id+"F0.wireOp",EDGE,"E2.top");var subQ10=sQuery(id+"F0.wireOp",EDGE,"E2.bottom");var subQ11=sQuery(id+"F0.wireOp",EDGE,"E1.right");var subQ12=sQuery(id+"F0.wireOp",EDGE,"E1.top");var subQ13=sQuery(id+"F0.wireOp",EDGE,"E1.bottom");var subQ14=sQuery(id+"F0.wireOp",EDGE,"E0");var subQ16=sQuery(id+"F4.wireOp",EDGE,"E7");var subQ17=makeQuery(id+"F5.opExtrude","SWEPT_FACE",FACE,{"disambiguationData":[OSD([subQ16])]});var subQ18=sQuery(id+"F4.wireOp",EDGE,"E8");var subQ20=sQuery(id+"F7.wireOp",EDGE,"E11.top");var subQ21=makeQuery(id+"F1.opExtrude","CAP_FACE",FACE,{"disambiguationData":[OSD([subQ14,subQ13,subQ12,subQ11,subQ10,subQ9,subQ8,subQ7,subQ6,subQ5,subQ4,subQ3,subQ2])],"isStart":true});var subQ22=makeQuery(id+"F5.boolean.opBoolean","SPLIT",EDGE,{"disambiguationData":[TD([subQ21])],"derivedFrom":makeQuery(id+"F5.opExtrude","CAP_EDGE",EDGE,{"disambiguationData":[OSD([subQ16])],"isStart":true})});var subQ23=sQuery(id+"F7.wireOp",EDGE,"E11.bottom");var subQ24=makeQuery(id+"F10.boolean.opBoolean","MERGE",FACE,{"derivedFrom":[subQ17,makeQuery(id+"F10.opExtrude","SWEPT_FACE",FACE,{"disambiguationData":[OSD([subQ16]),TDD([makeQuery(id+"F8.boolean.opBoolean","SPLIT",EDGE,{"disambiguationData":[TD([makeQuery(id+"F8.opExtrude","SWEPT_FACE",FACE,{"disambiguationData":[OSD([subQ23])]})])],"derivedFrom":subQ22})])]}),makeQuery(id+"F10.opExtrude","SWEPT_FACE",FACE,{"disambiguationData":[OSD([subQ16]),TDD([makeQuery(id+"F8.boolean.opBoolean","SPLIT",EDGE,{"disambiguationData":[TD([makeQuery(id+"F8.opExtrude","SWEPT_FACE",FACE,{"disambiguationData":[OSD([subQ20])]})])],"derivedFrom":subQ22})])]})]});var subQ25=sQuery(id+"F7.wireOp",EDGE,"E10.right");var subQ26=sQuery(id+"F7.wireOp",EDGE,"E10.top");var subQ27=sQuery(id+"F7.wireOp",EDGE,"E10.bottom");var subQ28=sQuery(id+"F7.wireOp",EDGE,"E9.right");var subQ29=sQuery(id+"F7.wireOp",EDGE,"E9.top");var subQ30=sQuery(id+"F7.wireOp",EDGE,"E9.bottom");Q3=makeQuery(id+"F20.boolean.opBoolean","MERGE",EDGE,{"derivedFrom":[makeQuery(id+"F16.boolean.opBoolean","INTERSECT",EDGE,{"disambiguationData":[OD(0.0)],"derivedFrom":[subQ24,subQ1]}),makeQuery(id+"F16.boolean.opBoolean","INTERSECT",EDGE,{"disambiguationData":[OD(2.0)],"derivedFrom":[subQ24,subQ1]}),makeQuery(id+"F16.boolean.opBoolean","INTERSECT",EDGE,{"disambiguationData":[OD(3.0)],"derivedFrom":[subQ24,subQ1]}),makeQuery(id+"F20.opExtrude","SWEPT_EDGE",EDGE,{"disambiguationData":[OSD([subQ6,subQ3,subQ2,subQ16,subQ18,subQ30,subQ29,subQ28,subQ27,subQ26,subQ25,subQ23,subQ20,subQ0]),TDD([makeQuery(id+"F16.boolean.opBoolean","INTERSECT",VERTEX,{"disambiguationData":[OD(1.0)],"derivedFrom":[makeQuery(id+"F9.boolean.opBoolean","MERGE",FACE,{"derivedFrom":[makeQuery(id+"F5.opExtrude","CAP_FACE",FACE,{"disambiguationData":[OSD([subQ6,subQ3,subQ2,subQ16,subQ18])],"isStart":false}),makeQuery(id+"F9.opExtrude","CAP_FACE",FACE,{"disambiguationData":[OSD([subQ16,subQ30,subQ29,subQ28,subQ23])],"isStart":false}),makeQuery(id+"F9.opExtrude","CAP_FACE",FACE,{"disambiguationData":[OSD([subQ16,subQ27,subQ26,subQ25,subQ20])],"isStart":false})]}),subQ24,subQ1]})])]})]});}
            fillet(context, id + "F21", {"entities" : qUnion([Q0, Q1, Q2, Q3]), "radius" : 5 * mm, "tangentPropagation" : true, "allowEdgeOverflow" : false});
        }
        {
            var Q0;
            Q0=makeQuery(id+"F16.opExtrude","SWEPT_FACE",FACE,{"disambiguationData":[OSD([sQuery(id+"F14.wireOp",EDGE,"E15.right")])]});
            var sketch = newSketch(context, id + "F22", { "sketchPlane" : qUnion([Q0])});
            skText(sketch, "E39", { "text": "Qmetrix", "fontName": "OpenSans-Regular.ttf"});
            const initialGuessF22  = {"E39": [-0.025, 0.0054, 1, 0, 0.0095]};
            skSetInitialGuess(sketch, initialGuessF22);
            skSolve(sketch);
        }
        {
            var Q0;
            Q0 = qSketchRegion(id + "F22", true);
            extrude(context, id + "F23", {"entities" : qUnion([Q0]), "operationType" : NewBodyOperationType.REMOVE, "oppositeDirection" : true, "depth" : 1 * mm});
        }
        {
            var Q0;
            Q0=qSketchRegion(id+"F11",true);
            extrude(context, id + "F24", {"entities" : qUnion([Q0]), "operationType" : NewBodyOperationType.REMOVE, "oppositeDirection" : true, "depth" : 25 * mm});
        }
        {
            var Q0;
            Q0=qSketchRegion(id+"F13",true);
            extrude(context, id + "F25", {"entities" : qUnion([Q0]), "operationType" : NewBodyOperationType.REMOVE, "oppositeDirection" : true, "depth" : 1 * mm});
        }
        {
            var Q0;
            Q0=makeQuery(id+"F16.opExtrude","SWEPT_FACE",FACE,{"disambiguationData":[OSD([sQuery(id+"F14.wireOp",EDGE,"E15.left")])]});
            var sketch = newSketch(context, id + "F26", { "sketchPlane" : qUnion([Q0])});
            skArc(sketch, "E40.0", {"start": v(-6.67, -28.09) * mm, "mid": v(-17.32, -33.09) * mm, "end": v(-6.67, -38.09) * mm});
            skLineSegment(sketch, "E40.1", {"start": v(-6.67, -28.09) * mm, "end": v(0.59, -28.09) * mm});
            skArc(sketch, "E40.2", {"start": v(0.59, -38.09) * mm, "mid": v(5.59, -33.09) * mm, "end": v(0.59, -28.09) * mm});
            skLineSegment(sketch, "E40.3", {"start": v(-6.67, -38.09) * mm, "end": v(0.59, -38.09) * mm});
            skArc(sketch, "E41.0", {"start": v(-37.5, 17.25) * mm, "mid": v(-42.5, 27.9) * mm, "end": v(-47.5, 17.25) * mm});
            skLineSegment(sketch, "E41.1", {"start": v(-37.5, 17.25) * mm, "end": v(-37.5, 10) * mm});
            skArc(sketch, "E41.2", {"start": v(-47.5, 10) * mm, "mid": v(-42.5, 5) * mm, "end": v(-37.5, 10) * mm});
            skLineSegment(sketch, "E41.3", {"start": v(-47.5, 17.25) * mm, "end": v(-47.5, 10) * mm});
            skArc(sketch, "E42.0", {"start": v(-53.73, 70) * mm, "mid": v(-57.27, 68.54) * mm, "end": v(-58.73, 65) * mm});
            skLineSegment(sketch, "E42.1", {"start": v(56.27, 70) * mm, "end": v(-53.73, 70) * mm});
            skLineSegment(sketch, "E42.2", {"start": v(-58.73, 65) * mm, "end": v(-58.73, -45) * mm});
            skArc(sketch, "E42.3", {"start": v(61.27, 65) * mm, "mid": v(59.8, 68.54) * mm, "end": v(56.27, 70) * mm});
            skArc(sketch, "E42.4", {"start": v(-58.73, -45) * mm, "mid": v(-57.27, -48.54) * mm, "end": v(-53.73, -50) * mm});
            skLineSegment(sketch, "E42.5", {"start": v(-53.73, -50) * mm, "end": v(56.27, -50) * mm});
            skArc(sketch, "E42.6", {"start": v(56.27, -50) * mm, "mid": v(59.8, -48.54) * mm, "end": v(61.27, -45) * mm});
            skLineSegment(sketch, "E42.7", {"start": v(61.27, -45) * mm, "end": v(61.27, 65) * mm});
            skLineSegment(sketch, "E43.0", {"start": v(-6.67, 46.91) * mm, "end": v(0.76, 46.91) * mm});
            skArc(sketch, "E43.1", {"start": v(-6.67, 56.91) * mm, "mid": v(-17.32, 51.91) * mm, "end": v(-6.67, 46.91) * mm});
            skLineSegment(sketch, "E43.2", {"start": v(-6.67, 56.91) * mm, "end": v(-0.17, 56.91) * mm});
            skArc(sketch, "E43.3", {"start": v(0.76, 46.91) * mm, "mid": v(5.3, 52.38) * mm, "end": v(-0.17, 56.91) * mm});
            skLineSegment(sketch, "E44.0", {"start": v(37.5, 17.25) * mm, "end": v(37.5, 10) * mm});
            skArc(sketch, "E44.1", {"start": v(47.5, 17.25) * mm, "mid": v(42.5, 27.9) * mm, "end": v(37.5, 17.25) * mm});
            skLineSegment(sketch, "E44.2", {"start": v(47.5, 17.25) * mm, "end": v(47.5, 10) * mm});
            skArc(sketch, "E44.3", {"start": v(37.5, 10) * mm, "mid": v(42.5, 5) * mm, "end": v(47.5, 10) * mm});
            skLineSegment(sketch, "E45", {"start": v(74.1, 51.91) * mm, "end": v(-89.68, 51.91) * mm, "construction": true});
            skLineSegment(sketch, "E46", {"start": v(77.77, -33.09) * mm, "end": v(-83.07, -33.09) * mm, "construction": true});
            skPoint(sketch, "E46.startSnap0", {"position": v(5.59, -33.09) * mm});
            skLineSegment(sketch, "E47", {"start": v(42.5, 85.53) * mm, "end": v(42.5, -77.77) * mm, "construction": true});
            skLineSegment(sketch, "E48", {"start": v(-42.5, 86.75) * mm, "end": v(-42.5, -90.74) * mm, "construction": true});
            skLineSegment(sketch, "E49.rect.bottom", {"start": v(40, 46.91) * mm, "end": v(45, 46.91) * mm});
            skLineSegment(sketch, "E49.rect.top", {"start": v(40, 56.91) * mm, "end": v(45, 56.91) * mm});
            skLineSegment(sketch, "E49.rect.left", {"start": v(40, 46.91) * mm, "end": v(40, 56.91) * mm});
            skLineSegment(sketch, "E49.rect.right", {"start": v(45, 46.91) * mm, "end": v(45, 56.91) * mm});
            skPoint(sketch, "E49.rect.middle", {"position": v(42.5, 51.91) * mm});
            skLineSegment(sketch, "E50.rect.bottom", {"start": v(40, -38.09) * mm, "end": v(45, -38.09) * mm});
            skLineSegment(sketch, "E50.rect.top", {"start": v(40, -28.09) * mm, "end": v(45, -28.09) * mm});
            skLineSegment(sketch, "E50.rect.left", {"start": v(40, -38.09) * mm, "end": v(40, -28.09) * mm});
            skLineSegment(sketch, "E50.rect.right", {"start": v(45, -38.09) * mm, "end": v(45, -28.09) * mm});
            skPoint(sketch, "E50.rect.middle", {"position": v(42.5, -33.09) * mm});
            skPoint(sketch, "E51.rect.middle", {"position": v(-42.5, -33.09) * mm});
            skLineSegment(sketch, "E52.rect.bottom", {"start": v(-45, 46.91) * mm, "end": v(-40, 46.91) * mm});
            skLineSegment(sketch, "E52.rect.top", {"start": v(-45, 56.91) * mm, "end": v(-40, 56.91) * mm});
            skLineSegment(sketch, "E52.rect.left", {"start": v(-45, 46.91) * mm, "end": v(-45, 56.91) * mm});
            skLineSegment(sketch, "E52.rect.right", {"start": v(-40, 46.91) * mm, "end": v(-40, 56.91) * mm});
            skPoint(sketch, "E52.rect.middle", {"position": v(-42.5, 51.91) * mm});
            skLineSegment(sketch, "E53.rect.bottom", {"start": v(-40, -28.09) * mm, "end": v(-45, -28.09) * mm});
            skLineSegment(sketch, "E53.rect.top", {"start": v(-40, -38.09) * mm, "end": v(-45, -38.09) * mm});
            skLineSegment(sketch, "E53.rect.left", {"start": v(-40, -28.09) * mm, "end": v(-40, -38.09) * mm});
            skLineSegment(sketch, "E53.rect.right", {"start": v(-45, -28.09) * mm, "end": v(-45, -38.09) * mm});
            skSolve(sketch);
        }
        {
            var Q0;
            Q0=makeQuery(id+"F26.imprint","IMPRINT",FACE,{"disambiguationData":[TD([[makeQuery(id+"F26.imprint","IMPRINT",EDGE,{"derivedFrom":sQuery(id+"F26.wireOp",EDGE,"E40.0")}),1.0]])]});
            var Q1;
            Q1=makeQuery(id+"F26.imprint","IMPRINT",FACE,{"disambiguationData":[TD([[makeQuery(id+"F26.imprint","IMPRINT",EDGE,{"derivedFrom":sQuery(id+"F26.wireOp",EDGE,"E44.0")}),1.0]])]});
            var Q2;
            Q2=makeQuery(id+"F26.imprint","IMPRINT",FACE,{"disambiguationData":[TD([[makeQuery(id+"F26.imprint","IMPRINT",EDGE,{"derivedFrom":sQuery(id+"F26.wireOp",EDGE,"E43.0")}),1.0]])]});
            var Q3;
            Q3=makeQuery(id+"F26.imprint","IMPRINT",FACE,{"disambiguationData":[TD([[makeQuery(id+"F26.imprint","IMPRINT",EDGE,{"derivedFrom":sQuery(id+"F26.wireOp",EDGE,"E41.0")}),1.0]])]});
            extrude(context, id + "F27", {"entities" : qUnion([Q0, Q1, Q2, Q3]), "operationType" : NewBodyOperationType.REMOVE, "oppositeDirection" : true, "depth" : 2 * mm});
        }
        {
            var Q0;
            Q0=makeQuery(id+"F16.opExtrude","SWEPT_FACE",FACE,{"disambiguationData":[OSD([sQuery(id+"F14.wireOp",EDGE,"E15.left")])]});
            var sketch = newSketch(context, id + "F28", { "sketchPlane" : qUnion([Q0])});
            skLineSegment(sketch, "E54.rect.bottom", {"start": v(37.8, 50.25) * mm, "end": v(47.2, 50.25) * mm});
            skLineSegment(sketch, "E54.rect.top", {"start": v(37.8, 54.5) * mm, "end": v(47.2, 54.5) * mm});
            skLineSegment(sketch, "E54.rect.left", {"start": v(37.8, 50.25) * mm, "end": v(37.8, 54.5) * mm});
            skLineSegment(sketch, "E54.rect.right", {"start": v(47.2, 50.25) * mm, "end": v(47.2, 54.5) * mm});
            skPoint(sketch, "E54.rect.middle", {"position": v(42.5, 52.38) * mm});
            skPoint(sketch, "E54.rect.middle.positionSnap0", {"position": v(42.5, 27.9) * mm});
            skPoint(sketch, "E54.rect.middle.positionSnap1", {"position": v(5.3, 52.38) * mm});
            skPoint(sketch, "E54.rect.centerSnap0", {"position": v(42.5, 27.9) * mm});
            skPoint(sketch, "E54.rect.centerSnap1", {"position": v(5.3, 52.38) * mm});
            skLineSegment(sketch, "E55.0.1.0", {"start": v(37.8, -34.82) * mm, "end": v(47.2, -34.82) * mm});
            skLineSegment(sketch, "E55.0.1.1", {"start": v(37.8, -30.56) * mm, "end": v(47.2, -30.56) * mm});
            skLineSegment(sketch, "E55.0.1.2", {"start": v(47.2, -34.82) * mm, "end": v(47.2, -30.56) * mm});
            skLineSegment(sketch, "E55.0.1.3", {"start": v(37.8, -34.82) * mm, "end": v(37.8, -30.56) * mm});
            skLineSegment(sketch, "E55.1.0.0", {"start": v(-43.45, 50.25) * mm, "end": v(-34.07, 50.25) * mm});
            skLineSegment(sketch, "E55.1.0.1", {"start": v(-43.45, 54.5) * mm, "end": v(-34.07, 54.5) * mm});
            skLineSegment(sketch, "E55.1.0.2", {"start": v(-34.07, 50.25) * mm, "end": v(-34.07, 54.5) * mm});
            skLineSegment(sketch, "E55.1.0.3", {"start": v(-43.45, 50.25) * mm, "end": v(-43.45, 54.5) * mm});
            skLineSegment(sketch, "E55.1.1.0", {"start": v(-43.45, -34.82) * mm, "end": v(-34.07, -34.82) * mm});
            skLineSegment(sketch, "E55.1.1.1", {"start": v(-43.45, -30.56) * mm, "end": v(-34.07, -30.56) * mm});
            skLineSegment(sketch, "E55.1.1.2", {"start": v(-34.07, -34.82) * mm, "end": v(-34.07, -30.56) * mm});
            skLineSegment(sketch, "E55.1.1.3", {"start": v(-43.45, -34.82) * mm, "end": v(-43.45, -30.56) * mm});
            skLineSegment(sketch, "E55.direction1", {"start": v(37.8, 50.25) * mm, "end": v(-43.45, 50.25) * mm, "construction": true});
            skLineSegment(sketch, "E55.direction2", {"start": v(37.8, 50.25) * mm, "end": v(37.8, -34.82) * mm, "construction": true});
            skSolve(sketch);
        }
        {
            var Q0;
            Q0 = qSketchRegion(id + "F28", true);
            extrude(context, id + "F29", {"entities" : qUnion([Q0]), "operationType" : NewBodyOperationType.ADD, "depth" : 6 * mm});
        }
        {
            var Q0;
            Q0=makeQuery(id+"F29.opExtrude","SWEPT_FACE",FACE,{"disambiguationData":[OSD([sQuery(id+"F28.wireOp",EDGE,"E54.rect.top")])]});
            var sketch = newSketch(context, id + "F30", { "sketchPlane" : qUnion([Q0])});
            skLineSegment(sketch, "E56.rect.bottom", {"start": v(17.53, 39.41) * mm, "end": v(14.64, 39.41) * mm});
            skLineSegment(sketch, "E56.rect.top", {"start": v(17.53, 45.59) * mm, "end": v(14.64, 45.59) * mm});
            skLineSegment(sketch, "E56.rect.left", {"start": v(17.53, 39.41) * mm, "end": v(17.53, 45.59) * mm});
            skLineSegment(sketch, "E56.rect.right", {"start": v(14.64, 39.41) * mm, "end": v(14.64, 45.59) * mm});
            skPoint(sketch, "E56.rect.middle", {"position": v(16.08, 42.5) * mm});
            skPoint(sketch, "E56.rect.middle.positionSnap0", {"position": v(16.08, 47.2) * mm});
            skPoint(sketch, "E56.rect.middle.positionSnap1", {"position": v(19.08, 42.5) * mm});
            skPoint(sketch, "E56.rect.centerSnap0", {"position": v(16.08, 47.2) * mm});
            skPoint(sketch, "E56.rect.centerSnap1", {"position": v(19.08, 42.5) * mm});
            skSolve(sketch);
        }
        {
            var Q0;
            Q0 = qSketchRegion(id + "F30", true);
            extrude(context, id + "F31", {"entities" : qUnion([Q0]), "operationType" : NewBodyOperationType.REMOVE, "oppositeDirection" : true, "depth" : 25 * mm});
        }
        {
            var Q0;
            Q0=makeQuery(id+"F29.opExtrude","SWEPT_FACE",FACE,{"disambiguationData":[OSD([sQuery(id+"F28.wireOp",EDGE,"E55.1.0.1")])]});
            var sketch = newSketch(context, id + "F32", { "sketchPlane" : qUnion([Q0])});
            skLineSegment(sketch, "E57.rect.bottom", {"start": v(17.38, -41.53) * mm, "end": v(14.79, -41.53) * mm});
            skLineSegment(sketch, "E57.rect.top", {"start": v(17.38, -36) * mm, "end": v(14.79, -36) * mm});
            skLineSegment(sketch, "E57.rect.left", {"start": v(17.38, -41.53) * mm, "end": v(17.38, -36) * mm});
            skLineSegment(sketch, "E57.rect.right", {"start": v(14.79, -41.53) * mm, "end": v(14.79, -36) * mm});
            skPoint(sketch, "E57.rect.middle", {"position": v(16.08, -38.76) * mm});
            skPoint(sketch, "E57.rect.middle.positionSnap0", {"position": v(19.08, -38.76) * mm});
            skPoint(sketch, "E57.rect.middle.positionSnap1", {"position": v(16.08, -34.07) * mm});
            skPoint(sketch, "E57.rect.centerSnap0", {"position": v(19.08, -38.76) * mm});
            skPoint(sketch, "E57.rect.centerSnap1", {"position": v(16.08, -34.07) * mm});
            skSolve(sketch);
        }
        {
            var Q0;
            Q0 = qSketchRegion(id + "F32", true);
            extrude(context, id + "F33", {"entities" : qUnion([Q0]), "operationType" : NewBodyOperationType.REMOVE, "oppositeDirection" : true, "depth" : 5 * mm});
        }
        {
            var Q0;
            Q0=makeQuery(id+"F29.opExtrude","SWEPT_FACE",FACE,{"disambiguationData":[OSD([sQuery(id+"F28.wireOp",EDGE,"E55.1.1.1")])]});
            var sketch = newSketch(context, id + "F34", { "sketchPlane" : qUnion([Q0])});
            skLineSegment(sketch, "E58.rect.bottom", {"start": v(17.4, -41.72) * mm, "end": v(14.78, -41.72) * mm});
            skLineSegment(sketch, "E58.rect.top", {"start": v(17.4, -35.8) * mm, "end": v(14.78, -35.8) * mm});
            skLineSegment(sketch, "E58.rect.left", {"start": v(17.4, -41.72) * mm, "end": v(17.4, -35.8) * mm});
            skLineSegment(sketch, "E58.rect.right", {"start": v(14.78, -41.72) * mm, "end": v(14.78, -35.8) * mm});
            skPoint(sketch, "E58.rect.middle", {"position": v(16.08, -38.76) * mm});
            skPoint(sketch, "E58.rect.middle.positionSnap0", {"position": v(19.08, -38.76) * mm});
            skPoint(sketch, "E58.rect.middle.positionSnap1", {"position": v(16.08, -34.07) * mm});
            skPoint(sketch, "E58.rect.centerSnap0", {"position": v(19.08, -38.76) * mm});
            skPoint(sketch, "E58.rect.centerSnap1", {"position": v(16.08, -34.07) * mm});
            skSolve(sketch);
        }
        {
            var Q0;
            Q0 = qSketchRegion(id + "F34", true);
            extrude(context, id + "F35", {"entities" : qUnion([Q0]), "operationType" : NewBodyOperationType.REMOVE, "oppositeDirection" : true, "depth" : 25 * mm});
        }
        {
            var Q0;
            Q0=makeQuery(id+"F29.opExtrude","SWEPT_FACE",FACE,{"disambiguationData":[OSD([sQuery(id+"F28.wireOp",EDGE,"E55.0.1.1")])]});
            var sketch = newSketch(context, id + "F36", { "sketchPlane" : qUnion([Q0])});
            skLineSegment(sketch, "E59.rect.bottom", {"start": v(17.44, 40.08) * mm, "end": v(14.72, 40.08) * mm});
            skLineSegment(sketch, "E59.rect.top", {"start": v(17.44, 44.92) * mm, "end": v(14.72, 44.92) * mm});
            skLineSegment(sketch, "E59.rect.left", {"start": v(17.44, 40.08) * mm, "end": v(17.44, 44.92) * mm});
            skLineSegment(sketch, "E59.rect.right", {"start": v(14.72, 40.08) * mm, "end": v(14.72, 44.92) * mm});
            skPoint(sketch, "E59.rect.middle", {"position": v(16.08, 42.5) * mm});
            skPoint(sketch, "E59.rect.middle.positionSnap0", {"position": v(19.08, 42.5) * mm});
            skPoint(sketch, "E59.rect.middle.positionSnap1", {"position": v(16.08, 47.2) * mm});
            skPoint(sketch, "E59.rect.centerSnap0", {"position": v(19.08, 42.5) * mm});
            skPoint(sketch, "E59.rect.centerSnap1", {"position": v(16.08, 47.2) * mm});
            skSolve(sketch);
        }
        {
            var Q0;
            Q0 = qSketchRegion(id + "F36", true);
            extrude(context, id + "F37", {"entities" : qUnion([Q0]), "operationType" : NewBodyOperationType.REMOVE, "oppositeDirection" : true, "depth" : 25 * mm});
        }
        {
            var Q0;
            Q0=makeQuery(id+"F16.opExtrude","SWEPT_FACE",FACE,{"disambiguationData":[OSD([sQuery(id+"F14.wireOp",EDGE,"E15.left")])]});
            var sketch = newSketch(context, id + "F38", { "sketchPlane" : qUnion([Q0])});
            skLineSegment(sketch, "E60.bottom", {"start": v(45.47, -38.15) * mm, "end": v(39.94, -38.15) * mm});
            skLineSegment(sketch, "E60.top", {"start": v(45.47, -36.11) * mm, "end": v(39.94, -36.11) * mm});
            skLineSegment(sketch, "E60.left", {"start": v(45.47, -38.15) * mm, "end": v(45.47, -36.11) * mm});
            skLineSegment(sketch, "E60.right", {"start": v(39.94, -38.15) * mm, "end": v(39.94, -36.11) * mm});
            skLineSegment(sketch, "E61.bottom", {"start": v(45.47, -29.12) * mm, "end": v(39.94, -29.12) * mm});
            skLineSegment(sketch, "E61.top", {"start": v(45.47, -27.23) * mm, "end": v(39.94, -27.23) * mm});
            skLineSegment(sketch, "E61.left", {"start": v(45.47, -29.12) * mm, "end": v(45.47, -27.23) * mm});
            skLineSegment(sketch, "E61.right", {"start": v(39.94, -29.12) * mm, "end": v(39.94, -27.23) * mm});
            skLineSegment(sketch, "E62.bottom", {"start": v(-35.9, -38.15) * mm, "end": v(-42.16, -38.15) * mm});
            skLineSegment(sketch, "E62.top", {"start": v(-35.9, -36.11) * mm, "end": v(-42.16, -36.11) * mm});
            skLineSegment(sketch, "E62.left", {"start": v(-35.9, -38.15) * mm, "end": v(-35.9, -36.11) * mm});
            skLineSegment(sketch, "E62.right", {"start": v(-42.16, -38.15) * mm, "end": v(-42.16, -36.11) * mm});
            skLineSegment(sketch, "E63.bottom", {"start": v(-35.9, -29.12) * mm, "end": v(-42.16, -29.12) * mm});
            skLineSegment(sketch, "E63.top", {"start": v(-35.9, -27.23) * mm, "end": v(-42.16, -27.23) * mm});
            skLineSegment(sketch, "E63.left", {"start": v(-35.9, -29.12) * mm, "end": v(-35.9, -27.23) * mm});
            skLineSegment(sketch, "E63.right", {"start": v(-42.16, -29.12) * mm, "end": v(-42.16, -27.23) * mm});
            skLineSegment(sketch, "E64.bottom", {"start": v(45.47, 46.86) * mm, "end": v(39.5, 46.86) * mm});
            skLineSegment(sketch, "E64.top", {"start": v(45.47, 48.9) * mm, "end": v(39.5, 48.9) * mm});
            skLineSegment(sketch, "E64.left", {"start": v(45.47, 46.86) * mm, "end": v(45.47, 48.9) * mm});
            skLineSegment(sketch, "E64.right", {"start": v(39.5, 46.86) * mm, "end": v(39.5, 48.9) * mm});
            skLineSegment(sketch, "E65.bottom", {"start": v(45.47, 55.89) * mm, "end": v(39.5, 55.89) * mm});
            skLineSegment(sketch, "E65.top", {"start": v(45.47, 58.22) * mm, "end": v(39.5, 58.22) * mm});
            skLineSegment(sketch, "E65.left", {"start": v(45.47, 55.89) * mm, "end": v(45.47, 58.22) * mm});
            skLineSegment(sketch, "E65.right", {"start": v(39.5, 55.89) * mm, "end": v(39.5, 58.22) * mm});
            skLineSegment(sketch, "E66.bottom", {"start": v(-35.9, 46.86) * mm, "end": v(-41.58, 46.86) * mm});
            skLineSegment(sketch, "E66.top", {"start": v(-35.9, 48.9) * mm, "end": v(-41.58, 48.9) * mm});
            skLineSegment(sketch, "E66.left", {"start": v(-35.9, 46.86) * mm, "end": v(-35.9, 48.9) * mm});
            skLineSegment(sketch, "E66.right", {"start": v(-41.58, 46.86) * mm, "end": v(-41.58, 48.9) * mm});
            skLineSegment(sketch, "E67.bottom", {"start": v(-35.9, 55.89) * mm, "end": v(-41.58, 55.89) * mm});
            skLineSegment(sketch, "E67.top", {"start": v(-35.9, 58.36) * mm, "end": v(-41.58, 58.36) * mm});
            skLineSegment(sketch, "E67.left", {"start": v(-35.9, 55.89) * mm, "end": v(-35.9, 58.36) * mm});
            skLineSegment(sketch, "E67.right", {"start": v(-41.58, 55.89) * mm, "end": v(-41.58, 58.36) * mm});
            skLineSegment(sketch, "E68.bottom", {"start": v(54.8, -20.78) * mm, "end": v(37.8, -20.78) * mm});
            skLineSegment(sketch, "E68.top", {"start": v(54.8, -13.78) * mm, "end": v(37.8, -13.78) * mm});
            skLineSegment(sketch, "E68.left", {"start": v(54.8, -20.78) * mm, "end": v(54.8, -13.78) * mm});
            skLineSegment(sketch, "E68.right", {"start": v(37.8, -20.78) * mm, "end": v(37.8, -13.78) * mm});
            skLineSegment(sketch, "E69.bottom", {"start": v(-34.9, -21.13) * mm, "end": v(-51.9, -21.13) * mm});
            skLineSegment(sketch, "E69.top", {"start": v(-34.9, -14.13) * mm, "end": v(-51.9, -14.13) * mm});
            skLineSegment(sketch, "E69.left", {"start": v(-34.9, -21.13) * mm, "end": v(-34.9, -14.13) * mm});
            skLineSegment(sketch, "E69.right", {"start": v(-51.9, -21.13) * mm, "end": v(-51.9, -14.13) * mm});
            skLineSegment(sketch, "E70.bottom", {"start": v(-34.9, 33.86) * mm, "end": v(-51.9, 33.86) * mm});
            skLineSegment(sketch, "E70.top", {"start": v(-34.9, 40.86) * mm, "end": v(-51.9, 40.86) * mm});
            skLineSegment(sketch, "E70.left", {"start": v(-34.9, 33.86) * mm, "end": v(-34.9, 40.86) * mm});
            skLineSegment(sketch, "E70.right", {"start": v(-51.9, 33.86) * mm, "end": v(-51.9, 40.86) * mm});
            skLineSegment(sketch, "E71.bottom", {"start": v(54.8, 33.86) * mm, "end": v(37.8, 33.86) * mm});
            skLineSegment(sketch, "E71.top", {"start": v(54.8, 40.86) * mm, "end": v(37.8, 40.86) * mm});
            skLineSegment(sketch, "E71.left", {"start": v(54.8, 33.86) * mm, "end": v(54.8, 40.86) * mm});
            skLineSegment(sketch, "E71.right", {"start": v(37.8, 33.86) * mm, "end": v(37.8, 40.86) * mm});
            skLineSegment(sketch, "E72.1.0", {"start": v(-29.02, -42.05) * mm, "end": v(-22.02, -42.05) * mm});
            skLineSegment(sketch, "E72.1.1", {"start": v(-29.02, -42.05) * mm, "end": v(-29.02, -25.05) * mm});
            skLineSegment(sketch, "E72.1.2", {"start": v(-29.02, -25.05) * mm, "end": v(-22.02, -25.05) * mm});
            skLineSegment(sketch, "E72.1.3", {"start": v(-22.02, -42.05) * mm, "end": v(-22.02, -25.05) * mm});
            skLineSegment(sketch, "E72.1.4", {"start": v(25.63, -42.05) * mm, "end": v(25.63, -25.05) * mm});
            skLineSegment(sketch, "E72.1.5", {"start": v(25.63, -42.05) * mm, "end": v(32.63, -42.05) * mm});
            skLineSegment(sketch, "E72.1.6", {"start": v(32.63, -42.05) * mm, "end": v(32.63, -25.05) * mm});
            skLineSegment(sketch, "E72.1.7", {"start": v(25.63, -25.05) * mm, "end": v(32.63, -25.05) * mm});
            skLineSegment(sketch, "E72.1.8", {"start": v(32.63, 47.66) * mm, "end": v(32.63, 64.66) * mm});
            skLineSegment(sketch, "E72.1.9", {"start": v(25.63, 47.66) * mm, "end": v(32.63, 47.66) * mm});
            skLineSegment(sketch, "E72.1.10", {"start": v(25.63, 47.66) * mm, "end": v(25.63, 64.66) * mm});
            skLineSegment(sketch, "E72.1.11", {"start": v(25.63, 64.66) * mm, "end": v(32.63, 64.66) * mm});
            skLineSegment(sketch, "E72.1.12", {"start": v(-22.37, 47.66) * mm, "end": v(-22.37, 64.66) * mm});
            skLineSegment(sketch, "E72.1.13", {"start": v(-29.37, 47.66) * mm, "end": v(-22.37, 47.66) * mm});
            skLineSegment(sketch, "E72.1.14", {"start": v(-29.37, 47.66) * mm, "end": v(-29.37, 64.66) * mm});
            skLineSegment(sketch, "E72.1.15", {"start": v(-29.37, 64.66) * mm, "end": v(-22.37, 64.66) * mm});
            skPoint(sketch, "E72.center", {"position": v(2.26, 10.5) * mm});
            skLineSegment(sketch, "E72.anchor1", {"start": v(2.26, 10.5) * mm, "end": v(54.8, -20.78) * mm, "construction": true});
            skLineSegment(sketch, "E72.anchor2", {"start": v(2.26, 10.5) * mm, "end": v(-29.02, -42.05) * mm, "construction": true});
            skSolve(sketch);
        }
        {
            var Q0;
            Q0=makeQuery(id+"F38.imprint","IMPRINT",FACE,{"disambiguationData":[TD([[makeQuery(id+"F38.imprint","IMPRINT",EDGE,{"derivedFrom":sQuery(id+"F38.wireOp",EDGE,"E60.bottom")}),-1.0]])]});
            var Q1;
            Q1=makeQuery(id+"F38.imprint","IMPRINT",FACE,{"disambiguationData":[TD([[makeQuery(id+"F38.imprint","IMPRINT",EDGE,{"derivedFrom":sQuery(id+"F38.wireOp",EDGE,"E61.bottom")}),-1.0]])]});
            var Q2;
            Q2=makeQuery(id+"F38.imprint","IMPRINT",FACE,{"disambiguationData":[TD([[makeQuery(id+"F38.imprint","IMPRINT",EDGE,{"derivedFrom":sQuery(id+"F38.wireOp",EDGE,"E63.bottom")}),-1.0]])]});
            var Q3;
            Q3=makeQuery(id+"F38.imprint","IMPRINT",FACE,{"disambiguationData":[TD([[makeQuery(id+"F38.imprint","IMPRINT",EDGE,{"derivedFrom":sQuery(id+"F38.wireOp",EDGE,"E62.bottom")}),-1.0]])]});
            var Q4;
            Q4=makeQuery(id+"F38.imprint","IMPRINT",FACE,{"disambiguationData":[TD([[makeQuery(id+"F38.imprint","IMPRINT",EDGE,{"derivedFrom":sQuery(id+"F38.wireOp",EDGE,"E66.bottom")}),-1.0]])]});
            var Q5;
            Q5=makeQuery(id+"F38.imprint","IMPRINT",FACE,{"disambiguationData":[TD([[makeQuery(id+"F38.imprint","IMPRINT",EDGE,{"derivedFrom":sQuery(id+"F38.wireOp",EDGE,"E67.bottom")}),-1.0]])]});
            var Q6;
            Q6=makeQuery(id+"F38.imprint","IMPRINT",FACE,{"disambiguationData":[TD([[makeQuery(id+"F38.imprint","IMPRINT",EDGE,{"derivedFrom":sQuery(id+"F38.wireOp",EDGE,"E65.bottom")}),-1.0]])]});
            var Q7;
            Q7=makeQuery(id+"F38.imprint","IMPRINT",FACE,{"disambiguationData":[TD([[makeQuery(id+"F38.imprint","IMPRINT",EDGE,{"derivedFrom":sQuery(id+"F38.wireOp",EDGE,"E64.bottom")}),-1.0]])]});
            var Q8;
            Q8=makeQuery(id+"F38.imprint","IMPRINT",FACE,{"disambiguationData":[TD([[makeQuery(id+"F38.imprint","IMPRINT",EDGE,{"derivedFrom":sQuery(id+"F38.wireOp",EDGE,"E68.bottom")}),-1.0]])]});
            var Q9;
            Q9=makeQuery(id+"F38.imprint","IMPRINT",FACE,{"disambiguationData":[TD([[makeQuery(id+"F38.imprint","IMPRINT",EDGE,{"derivedFrom":sQuery(id+"F38.wireOp",EDGE,"E71.bottom")}),-1.0]])]});
            var Q10;
            Q10=makeQuery(id+"F38.imprint","IMPRINT",FACE,{"disambiguationData":[TD([[makeQuery(id+"F38.imprint","IMPRINT",EDGE,{"derivedFrom":sQuery(id+"F38.wireOp",EDGE,"E69.bottom")}),-1.0]])]});
            var Q11;
            Q11=makeQuery(id+"F38.imprint","IMPRINT",FACE,{"disambiguationData":[TD([[makeQuery(id+"F38.imprint","IMPRINT",EDGE,{"derivedFrom":sQuery(id+"F38.wireOp",EDGE,"E70.bottom")}),-1.0]])]});
            var Q12;
            Q12=makeQuery(id+"F38.imprint","IMPRINT",FACE,{"disambiguationData":[TD([[makeQuery(id+"F38.imprint","IMPRINT",EDGE,{"derivedFrom":sQuery(id+"F38.wireOp",EDGE,"E72.1.4")}),-1.0]])]});
            var Q13;
            Q13=makeQuery(id+"F38.imprint","IMPRINT",FACE,{"disambiguationData":[TD([[makeQuery(id+"F38.imprint","IMPRINT",EDGE,{"derivedFrom":sQuery(id+"F38.wireOp",EDGE,"E72.1.0")}),1.0]])]});
            var Q14;
            Q14=makeQuery(id+"F38.imprint","IMPRINT",FACE,{"disambiguationData":[TD([[makeQuery(id+"F38.imprint","IMPRINT",EDGE,{"derivedFrom":sQuery(id+"F38.wireOp",EDGE,"E72.1.12")}),1.0]])]});
            var Q15;
            Q15=makeQuery(id+"F38.imprint","IMPRINT",FACE,{"disambiguationData":[TD([[makeQuery(id+"F38.imprint","IMPRINT",EDGE,{"derivedFrom":sQuery(id+"F38.wireOp",EDGE,"E72.1.8")}),1.0]])]});
            extrude(context, id + "F39", {"entities" : qUnion([Q0, Q1, Q2, Q3, Q4, Q5, Q6, Q7, Q8, Q9, Q10, Q11, Q12, Q13, Q14, Q15]), "operationType" : NewBodyOperationType.REMOVE, "oppositeDirection" : true, "depth" : 25 * mm});
        }
        {
            var Q0;
            Q0=makeQuery(id+"F16.opExtrude","SWEPT_FACE",FACE,{"disambiguationData":[OSD([sQuery(id+"F14.wireOp",EDGE,"E15.left")])]});
            var sketch = newSketch(context, id + "F40", { "sketchPlane" : qUnion([Q0])});
            skCircle(sketch, "E73", {"center": v(29.13, -17.28) * mm, "radius": 2.5 * mm});
            skPoint(sketch, "E73.centerSnap0", {"position": v(37.8, -17.28) * mm});
            skPoint(sketch, "E73.centerSnap1", {"position": v(29.13, -25.05) * mm});
            skCircle(sketch, "E74", {"center": v(-25.52, -17.63) * mm, "radius": 2.5 * mm});
            skPoint(sketch, "E74.centerSnap0", {"position": v(-34.9, -17.63) * mm});
            skPoint(sketch, "E74.centerSnap1", {"position": v(-25.52, -25.05) * mm});
            skCircle(sketch, "E75", {"center": v(-25.87, 37.36) * mm, "radius": 2.5 * mm});
            skPoint(sketch, "E75.centerSnap0", {"position": v(-25.87, 47.66) * mm});
            skPoint(sketch, "E75.centerSnap1", {"position": v(-34.9, 37.36) * mm});
            skCircle(sketch, "E76", {"center": v(29.13, 37.36) * mm, "radius": 2.5 * mm});
            skPoint(sketch, "E76.centerSnap0", {"position": v(37.8, 37.36) * mm});
            skPoint(sketch, "E76.centerSnap1", {"position": v(29.13, 47.66) * mm});
            skSolve(sketch);
        }
        {
            var Q0;
            Q0=makeQuery(id+"F40.imprint","IMPRINT",FACE,{"disambiguationData":[TD([[makeQuery(id+"F40.imprint","IMPRINT",EDGE,{"derivedFrom":sQuery(id+"F40.wireOp",EDGE,"E73")}),1.0]])]});
            var Q1;
            Q1=makeQuery(id+"F40.imprint","IMPRINT",FACE,{"disambiguationData":[TD([[makeQuery(id+"F40.imprint","IMPRINT",EDGE,{"derivedFrom":sQuery(id+"F40.wireOp",EDGE,"E74")}),1.0]])]});
            var Q2;
            Q2=makeQuery(id+"F40.imprint","IMPRINT",FACE,{"disambiguationData":[TD([[makeQuery(id+"F40.imprint","IMPRINT",EDGE,{"derivedFrom":sQuery(id+"F40.wireOp",EDGE,"E75")}),1.0]])]});
            var Q3;
            Q3=makeQuery(id+"F40.imprint","IMPRINT",FACE,{"disambiguationData":[TD([[makeQuery(id+"F40.imprint","IMPRINT",EDGE,{"derivedFrom":sQuery(id+"F40.wireOp",EDGE,"E76")}),1.0]])]});
            var Q4;
            Q4=sQuery(id+"F40.wireOp",EDGE,"E73");
            var Q5;
            Q5=sQuery(id+"F40.wireOp",EDGE,"E74");
            var Q6;
            Q6=sQuery(id+"F40.wireOp",EDGE,"E75");
            var Q7;
            Q7=sQuery(id+"F40.wireOp",EDGE,"E76");
            extrude(context, id + "F41", {"entities" : qUnion([Q0, Q1, Q2, Q3]), "operationType" : NewBodyOperationType.REMOVE, "surfaceEntities" : qUnion([Q4, Q5, Q6, Q7]), "oppositeDirection" : true, "depth" : 25 * mm});
        }
        {
            var Q0;
            Q0=makeQuery(id+"F16.opExtrude","CAP_EDGE",EDGE,{"disambiguationData":[OSD([sQuery(id+"F14.wireOp",EDGE,"E15.left")])],"isStart":false});
            var Q1;
            {var subQ1=sQuery(id+"F7.wireOp",EDGE,"E10.top");var subQ2=sQuery(id+"F4.wireOp",EDGE,"E7");Q1=makeQuery(id+"F16.boolean.opBoolean","SPLIT",EDGE,{"disambiguationData":[TD([makeQuery(id+"F9.opExtrude","SWEPT_FACE",FACE,{"disambiguationData":[OSD([subQ1])]})])],"derivedFrom":makeQuery(id+"F5.opExtrude","CAP_EDGE",EDGE,{"disambiguationData":[OSD([subQ2])],"isStart":false})});}
            var Q2;
            Q2=makeQuery(id+"F9.opExtrude","CAP_EDGE",EDGE,{"disambiguationData":[OSD([sQuery(id+"F7.wireOp",EDGE,"E10.top")])],"isStart":false});
            var Q3;
            {var subQ0=sQuery(id+"F7.wireOp",EDGE,"E10.top");Q3=makeQuery(id+"F12.opFillet","BLEND_EDGE",EDGE,{"blendedFrom":[makeQuery(id+"F9.opExtrude","CAP_EDGE",EDGE,{"disambiguationData":[OSD([sQuery(id+"F7.wireOp",EDGE,"E10.right")])],"isStart":false}),makeQuery(id+"F10.boolean.opBoolean","MERGE",FACE,{"derivedFrom":[makeQuery(id+"F9.opExtrude","SWEPT_FACE",FACE,{"disambiguationData":[OSD([subQ0])]}),makeQuery(id+"F10.opExtrude","SWEPT_FACE",FACE,{"disambiguationData":[OSD([subQ0])]})]})],"blendedInto":[makeQuery(id+"F10.boolean.opBoolean","MERGE",FACE,{"derivedFrom":[makeQuery(id+"F9.opExtrude","SWEPT_FACE",FACE,{"disambiguationData":[OSD([subQ0])]}),makeQuery(id+"F10.opExtrude","SWEPT_FACE",FACE,{"disambiguationData":[OSD([subQ0])]})]})]});}
            var Q4;
            {var subQ0=sQuery(id+"F0.wireOp",EDGE,"E5.trimOffspring");var subQ1=sQuery(id+"F0.wireOp",EDGE,"E4.right");var subQ2=sQuery(id+"F0.wireOp",EDGE,"E4.left");var subQ3=sQuery(id+"F0.wireOp",EDGE,"E4.top");var subQ4=sQuery(id+"F0.wireOp",EDGE,"E4.bottom");var subQ5=sQuery(id+"F0.wireOp",EDGE,"E3.trimOffspring");var subQ6=sQuery(id+"F0.wireOp",EDGE,"E2.right");var subQ7=sQuery(id+"F0.wireOp",EDGE,"E2.top");var subQ8=sQuery(id+"F0.wireOp",EDGE,"E2.bottom");var subQ9=sQuery(id+"F0.wireOp",EDGE,"E1.right");var subQ10=sQuery(id+"F0.wireOp",EDGE,"E1.top");var subQ11=sQuery(id+"F0.wireOp",EDGE,"E1.bottom");var subQ12=sQuery(id+"F0.wireOp",EDGE,"E0");var subQ14=sQuery(id+"F4.wireOp",EDGE,"E7");Q4=makeQuery(id+"F10.opExtrude","CAP_EDGE",EDGE,{"disambiguationData":[OSD([subQ14]),TDD([makeQuery(id+"F8.boolean.opBoolean","SPLIT",EDGE,{"disambiguationData":[TD([makeQuery(id+"F8.opExtrude","SWEPT_FACE",FACE,{"disambiguationData":[OSD([sQuery(id+"F7.wireOp",EDGE,"E11.top")])]})])],"derivedFrom":makeQuery(id+"F5.boolean.opBoolean","SPLIT",EDGE,{"disambiguationData":[TD([makeQuery(id+"F1.opExtrude","CAP_FACE",FACE,{"disambiguationData":[OSD([subQ12,subQ11,subQ10,subQ9,subQ8,subQ7,subQ6,subQ5,subQ4,subQ3,subQ2,subQ1,subQ0])],"isStart":true})])],"derivedFrom":makeQuery(id+"F5.opExtrude","CAP_EDGE",EDGE,{"disambiguationData":[OSD([subQ14])],"isStart":true})})})])],"isStart":false});}
            var Q5;
            {var subQ0=sQuery(id+"F0.wireOp",EDGE,"E5.trimOffspring");var subQ1=sQuery(id+"F0.wireOp",EDGE,"E4.right");var subQ2=sQuery(id+"F0.wireOp",EDGE,"E4.left");var subQ3=sQuery(id+"F0.wireOp",EDGE,"E4.top");var subQ4=sQuery(id+"F0.wireOp",EDGE,"E4.bottom");var subQ5=sQuery(id+"F0.wireOp",EDGE,"E3.trimOffspring");var subQ6=sQuery(id+"F0.wireOp",EDGE,"E2.right");var subQ7=sQuery(id+"F0.wireOp",EDGE,"E2.top");var subQ8=sQuery(id+"F0.wireOp",EDGE,"E2.bottom");var subQ9=sQuery(id+"F0.wireOp",EDGE,"E1.right");var subQ10=sQuery(id+"F0.wireOp",EDGE,"E1.top");var subQ11=sQuery(id+"F0.wireOp",EDGE,"E1.bottom");var subQ12=sQuery(id+"F0.wireOp",EDGE,"E0");var subQ13=makeQuery(id+"F1.opExtrude","CAP_FACE",FACE,{"disambiguationData":[OSD([subQ12,subQ11,subQ10,subQ9,subQ8,subQ7,subQ6,subQ5,subQ4,subQ3,subQ2,subQ1,subQ0])],"isStart":true});var subQ14=sQuery(id+"F4.wireOp",EDGE,"E7");Q5=makeQuery(id+"F10.opExtrude","CAP_EDGE",EDGE,{"disambiguationData":[OSD([subQ14]),TDD([makeQuery(id+"F8.boolean.opBoolean","SPLIT",EDGE,{"disambiguationData":[TD([makeQuery(id+"F8.opExtrude","SWEPT_FACE",FACE,{"disambiguationData":[OSD([sQuery(id+"F7.wireOp",EDGE,"E11.bottom")])]})])],"derivedFrom":makeQuery(id+"F5.boolean.opBoolean","SPLIT",EDGE,{"disambiguationData":[TD([subQ13])],"derivedFrom":makeQuery(id+"F5.opExtrude","CAP_EDGE",EDGE,{"disambiguationData":[OSD([subQ14])],"isStart":true})})})])],"isStart":false});}
            var Q6;
            {var subQ0=sQuery(id+"F7.wireOp",EDGE,"E9.top");var subQ2=sQuery(id+"F4.wireOp",EDGE,"E7");Q6=makeQuery(id+"F16.boolean.opBoolean","SPLIT",EDGE,{"disambiguationData":[TD([makeQuery(id+"F9.opExtrude","SWEPT_FACE",FACE,{"disambiguationData":[OSD([subQ0])]})])],"derivedFrom":makeQuery(id+"F5.opExtrude","CAP_EDGE",EDGE,{"disambiguationData":[OSD([subQ2])],"isStart":false})});}
            var Q7;
            Q7=makeQuery(id+"F10.opExtrude","CAP_EDGE",EDGE,{"disambiguationData":[OSD([sQuery(id+"F7.wireOp",EDGE,"E9.top")])],"isStart":false});
            fillet(context, id + "F42", {"entities" : qUnion([Q0, Q1, Q2, Q3, Q4, Q5, Q6, Q7]), "radius" : 3 * mm, "tangentPropagation" : true, "allowEdgeOverflow" : false});
        }
    });
